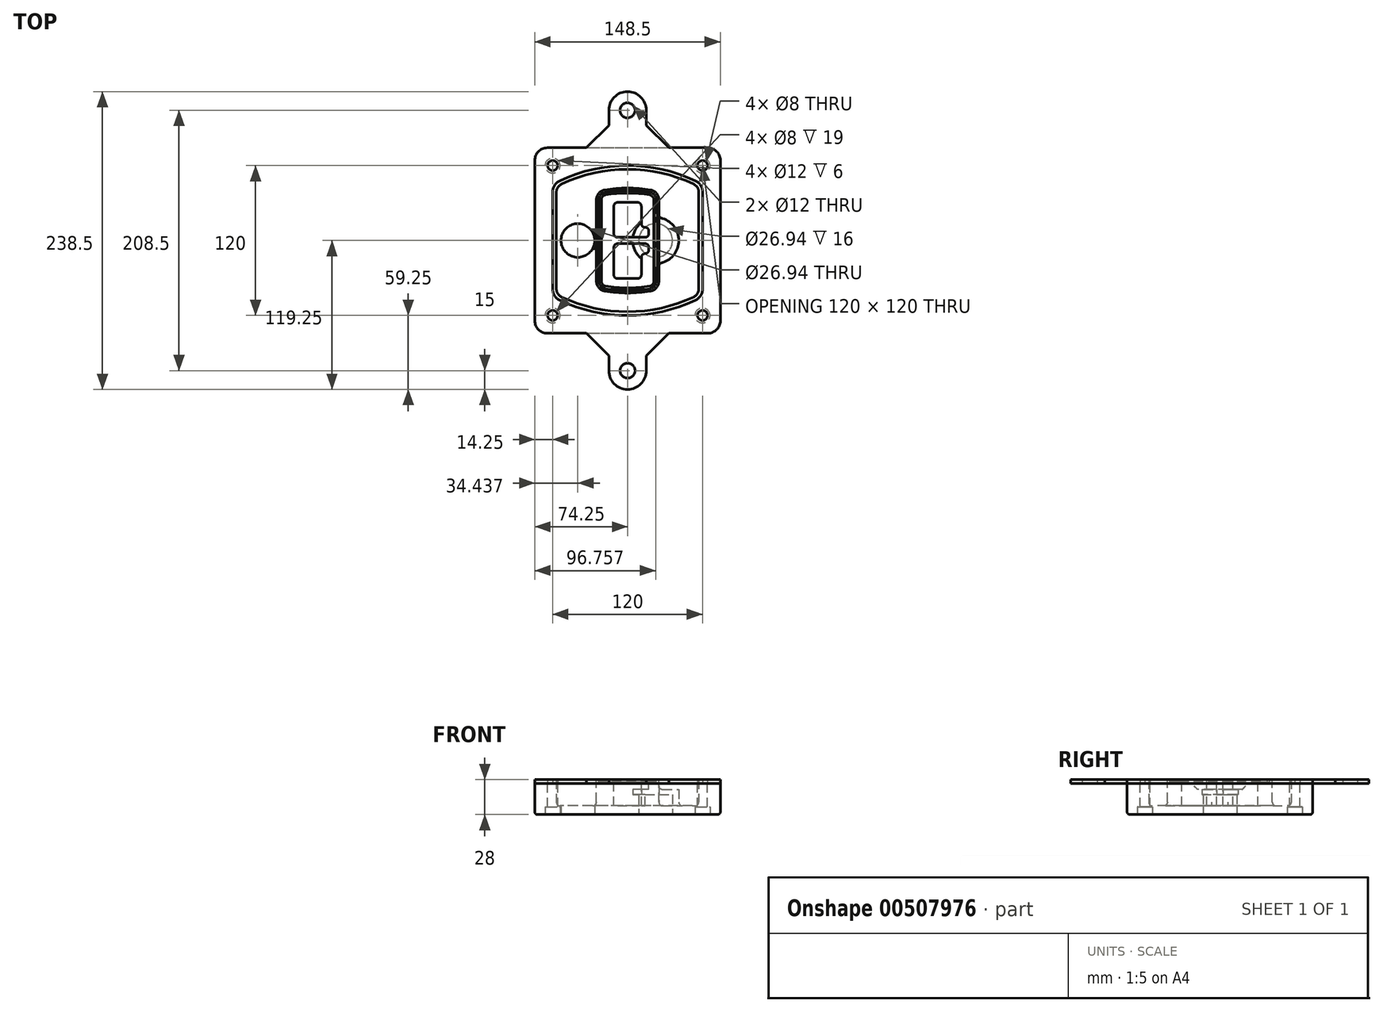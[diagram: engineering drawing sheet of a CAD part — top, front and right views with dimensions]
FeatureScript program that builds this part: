
annotation { "Feature Type Name" : "Feature", "Feature Type Description" : "" }
export const myFeature = defineFeature(function(context is Context, id is Id, definition is map)
    precondition{}
    {
        {
            var Q0;
            Q0=qCreatedBy(makeId("Top.planeOp"),FACE);
            var sketch = newSketch(context, id + "F0", { "sketchPlane" : qUnion([Q0])});
            skPoint(sketch, "E0.rect.middle", {"position": v(0, 0) * mm});
            skLineSegment(sketch, "E1.bottom", {"start": v(-64.25, -74.25) * mm, "end": v(64.25, -74.25) * mm});
            skLineSegment(sketch, "E1.top", {"start": v(-64.25, 74.25) * mm, "end": v(64.25, 74.25) * mm});
            skLineSegment(sketch, "E1.left", {"start": v(-74.25, -64.25) * mm, "end": v(-74.25, 64.25) * mm});
            skLineSegment(sketch, "E1.right", {"start": v(74.25, -64.25) * mm, "end": v(74.25, 64.25) * mm});
            skLineSegment(sketch, "E2", {"start": v(-74.25, 74.25) * mm, "end": v(74.25, -74.25) * mm, "construction": true});
            skLineSegment(sketch, "E3", {"start": v(74.25, 74.25) * mm, "end": v(-74.25, -74.25) * mm, "construction": true});
            skCircle(sketch, "E4", {"center": v(-60, 60) * mm, "radius": 4 * mm});
            skCircle(sketch, "E5", {"center": v(60, 60) * mm, "radius": 4 * mm});
            skCircle(sketch, "E6", {"center": v(60, -60) * mm, "radius": 4 * mm});
            skCircle(sketch, "E7", {"center": v(-60, -60) * mm, "radius": 4 * mm});
            skLineSegment(sketch, "E8", {"start": v(-60, 60) * mm, "end": v(60, 60) * mm, "construction": true});
            skLineSegment(sketch, "E9", {"start": v(60, 60) * mm, "end": v(60, -60) * mm, "construction": true});
            skLineSegment(sketch, "E10", {"start": v(60, -60) * mm, "end": v(-60, -60) * mm, "construction": true});
            skLineSegment(sketch, "E11", {"start": v(-60, -60) * mm, "end": v(-60, 60) * mm, "construction": true});
            skLineSegment(sketch, "E12", {"start": v(-60, 38.83) * mm, "end": v(-60, -38.83) * mm});
            skLineSegment(sketch, "E13", {"start": v(60, 38.83) * mm, "end": v(60, -38.83) * mm});
            skArc(sketch, "E14", {"start": v(54.26, 47.88) * mm, "mid": v(0, 60) * mm, "end": v(-54.26, 47.88) * mm});
            skArc(sketch, "E15", {"start": v(-54.26, -47.88) * mm, "mid": v(0, -60) * mm, "end": v(54.26, -47.88) * mm});
            skLineSegment(sketch, "E16", {"start": v(-60, 0) * mm, "end": v(60, 0) * mm, "construction": true});
            skPoint(sketch, "E17.visualSharp", {"position": v(-60, -45) * mm});
            skArc(sketch, "E17.filletArc", {"start": v(-60, -38.83) * mm, "mid": v(-58.44, -44.2) * mm, "end": v(-54.26, -47.88) * mm});
            skPoint(sketch, "E18.visualSharp", {"position": v(-60, 45) * mm});
            skArc(sketch, "E18.filletArc", {"start": v(-54.26, 47.88) * mm, "mid": v(-58.44, 44.2) * mm, "end": v(-60, 38.83) * mm});
            skPoint(sketch, "E19.visualSharp", {"position": v(60, 45) * mm});
            skArc(sketch, "E19.filletArc", {"start": v(60, 38.83) * mm, "mid": v(58.44, 44.2) * mm, "end": v(54.26, 47.88) * mm});
            skPoint(sketch, "E20.visualSharp", {"position": v(60, -45) * mm});
            skArc(sketch, "E20.filletArc", {"start": v(54.26, -47.88) * mm, "mid": v(58.44, -44.2) * mm, "end": v(60, -38.83) * mm});
            skPoint(sketch, "E21.visualSharp", {"position": v(-74.25, 74.25) * mm});
            skArc(sketch, "E21.filletArc", {"start": v(-64.25, 74.25) * mm, "mid": v(-71.32, 71.32) * mm, "end": v(-74.25, 64.25) * mm});
            skPoint(sketch, "E22.visualSharp", {"position": v(74.25, 74.25) * mm});
            skArc(sketch, "E22.filletArc", {"start": v(74.25, 64.25) * mm, "mid": v(71.32, 71.32) * mm, "end": v(64.25, 74.25) * mm});
            skPoint(sketch, "E23.visualSharp", {"position": v(74.25, -74.25) * mm});
            skArc(sketch, "E23.filletArc", {"start": v(64.25, -74.25) * mm, "mid": v(71.32, -71.32) * mm, "end": v(74.25, -64.25) * mm});
            skPoint(sketch, "E24.visualSharp", {"position": v(-74.25, -74.25) * mm});
            skArc(sketch, "E24.filletArc", {"start": v(-74.25, -64.25) * mm, "mid": v(-71.32, -71.32) * mm, "end": v(-64.25, -74.25) * mm});
            skArc(sketch, "E25.0", {"start": v(57, 38.83) * mm, "mid": v(55.9, 42.58) * mm, "end": v(52.98, 45.17) * mm});
            skLineSegment(sketch, "E25.1", {"start": v(57, 38.83) * mm, "end": v(57, -38.83) * mm});
            skArc(sketch, "E25.2", {"start": v(52.98, -45.17) * mm, "mid": v(55.9, -42.58) * mm, "end": v(57, -38.83) * mm});
            skArc(sketch, "E25.3", {"start": v(-52.98, -45.17) * mm, "mid": v(0, -57) * mm, "end": v(52.98, -45.17) * mm});
            skArc(sketch, "E25.4", {"start": v(-57, -38.83) * mm, "mid": v(-55.9, -42.58) * mm, "end": v(-52.98, -45.17) * mm});
            skArc(sketch, "E25.5", {"start": v(52.98, 45.17) * mm, "mid": v(0, 57) * mm, "end": v(-52.98, 45.17) * mm});
            skLineSegment(sketch, "E25.6", {"start": v(-57, 38.83) * mm, "end": v(-57, -38.83) * mm});
            skArc(sketch, "E25.7", {"start": v(-52.98, 45.17) * mm, "mid": v(-55.9, 42.58) * mm, "end": v(-57, 38.83) * mm});
            skArc(sketch, "E26.0", {"start": v(-55.96, 51.5) * mm, "mid": v(-61.82, 46.33) * mm, "end": v(-64, 38.83) * mm});
            skArc(sketch, "E26.1", {"start": v(55.96, 51.5) * mm, "mid": v(0, 64) * mm, "end": v(-55.96, 51.5) * mm});
            skArc(sketch, "E26.2", {"start": v(64, 38.83) * mm, "mid": v(61.82, 46.33) * mm, "end": v(55.96, 51.5) * mm});
            skLineSegment(sketch, "E26.3", {"start": v(64, 38.83) * mm, "end": v(64, -38.83) * mm});
            skArc(sketch, "E26.4", {"start": v(55.96, -51.5) * mm, "mid": v(61.82, -46.33) * mm, "end": v(64, -38.83) * mm});
            skLineSegment(sketch, "E26.5", {"start": v(-64, 38.83) * mm, "end": v(-64, -38.83) * mm});
            skArc(sketch, "E26.6", {"start": v(-55.96, -51.5) * mm, "mid": v(0, -64) * mm, "end": v(55.96, -51.5) * mm});
            skArc(sketch, "E26.7", {"start": v(-64, -38.83) * mm, "mid": v(-61.82, -46.33) * mm, "end": v(-55.96, -51.5) * mm});
            skSolve(sketch);
        }
        {
            var Q0;
            Q0=makeQuery(id+"F0.imprint","IMPRINT",FACE,{"disambiguationData":[TD([[makeQuery(id+"F0.imprint","IMPRINT",EDGE,{"derivedFrom":sQuery(id+"F0.wireOp",EDGE,"E1.bottom")}),1.0]])]});
            var Q1;
            Q1=makeQuery(id+"F0.imprint","IMPRINT",FACE,{"disambiguationData":[TD([[makeQuery(id+"F0.imprint","IMPRINT",EDGE,{"derivedFrom":sQuery(id+"F0.wireOp",EDGE,"E12")}),1.0]])]});
            var Q2;
            Q2=makeQuery(id+"F0.imprint","IMPRINT",FACE,{"disambiguationData":[TD([[makeQuery(id+"F0.imprint","IMPRINT",EDGE,{"derivedFrom":sQuery(id+"F0.wireOp",EDGE,"E25.0")}),1.0]])]});
            var Q3;
            Q3=makeQuery(id+"F0.imprint","IMPRINT",FACE,{"disambiguationData":[TD([[makeQuery(id+"F0.imprint","IMPRINT",EDGE,{"derivedFrom":sQuery(id+"F0.wireOp",EDGE,"E12")}),-1.0]])]});
            extrude(context, id + "F1", {"entities" : qUnion([Q0, Q1, Q2, Q3]), "oppositeDirection" : true, "depth" : 25 * mm});
        }
        {
            var Q0;
            Q0=makeQuery(id+"F0.imprint","IMPRINT",FACE,{"disambiguationData":[TD([[makeQuery(id+"F0.imprint","IMPRINT",EDGE,{"derivedFrom":sQuery(id+"F0.wireOp",EDGE,"E12")}),1.0]])]});
            extrude(context, id + "F2", {"entities" : qUnion([Q0]), "operationType" : NewBodyOperationType.ADD, "depth" : 3 * mm});
        }
        {
            var Q0;
            Q0=makeQuery(id+"F0.imprint","IMPRINT",FACE,{"disambiguationData":[TD([[makeQuery(id+"F0.imprint","IMPRINT",EDGE,{"derivedFrom":sQuery(id+"F0.wireOp",EDGE,"E25.0")}),1.0]])]});
            extrude(context, id + "F3", {"entities" : qUnion([Q0]), "operationType" : NewBodyOperationType.REMOVE, "oppositeDirection" : true, "depth" : 18 * mm});
        }
        {
            var Q0;
            Q0=makeQuery(id+"F2.opExtrude","CAP_FACE",FACE,{"disambiguationData":[OSD([sQuery(id+"F0.wireOp",EDGE,"E12"),sQuery(id+"F0.wireOp",EDGE,"E13"),sQuery(id+"F0.wireOp",EDGE,"E14"),sQuery(id+"F0.wireOp",EDGE,"E15"),sQuery(id+"F0.wireOp",EDGE,"E17.filletArc"),sQuery(id+"F0.wireOp",EDGE,"E18.filletArc"),sQuery(id+"F0.wireOp",EDGE,"E19.filletArc"),sQuery(id+"F0.wireOp",EDGE,"E20.filletArc"),sQuery(id+"F0.wireOp",EDGE,"E25.0"),sQuery(id+"F0.wireOp",EDGE,"E25.1"),sQuery(id+"F0.wireOp",EDGE,"E25.2"),sQuery(id+"F0.wireOp",EDGE,"E25.3"),sQuery(id+"F0.wireOp",EDGE,"E25.4"),sQuery(id+"F0.wireOp",EDGE,"E25.5"),sQuery(id+"F0.wireOp",EDGE,"E25.6"),sQuery(id+"F0.wireOp",EDGE,"E25.7")])],"isStart":false});
            var sketch = newSketch(context, id + "F4", { "sketchPlane" : qUnion([Q0])});
            skArc(sketch, "E27.0", {"start": v(-18.34, -40.45) * mm, "mid": v(0, -42) * mm, "end": v(18.34, -40.45) * mm});
            skArc(sketch, "E28.0", {"start": v(18.34, 40.45) * mm, "mid": v(0, 42) * mm, "end": v(-18.34, 40.45) * mm});
            skLineSegment(sketch, "E29", {"start": v(-25, 32.57) * mm, "end": v(-25, -32.57) * mm});
            skLineSegment(sketch, "E30", {"start": v(25, 32.57) * mm, "end": v(25, -32.57) * mm});
            skLineSegment(sketch, "E31", {"start": v(-25, 39.1) * mm, "end": v(25, 39.1) * mm, "construction": true});
            skLineSegment(sketch, "E32", {"start": v(-25, -39.1) * mm, "end": v(25, -39.1) * mm, "construction": true});
            skPoint(sketch, "E33.visualSharp", {"position": v(-25, 39.1) * mm});
            skArc(sketch, "E33.filletArc", {"start": v(-18.34, 40.45) * mm, "mid": v(-23.11, 37.73) * mm, "end": v(-25, 32.57) * mm});
            skPoint(sketch, "E34.visualSharp", {"position": v(25, 39.1) * mm});
            skArc(sketch, "E34.filletArc", {"start": v(25, 32.57) * mm, "mid": v(23.11, 37.73) * mm, "end": v(18.34, 40.45) * mm});
            skPoint(sketch, "E35.visualSharp", {"position": v(25, -39.1) * mm});
            skArc(sketch, "E35.filletArc", {"start": v(18.34, -40.45) * mm, "mid": v(23.11, -37.73) * mm, "end": v(25, -32.57) * mm});
            skPoint(sketch, "E36.visualSharp", {"position": v(-25, -39.1) * mm});
            skArc(sketch, "E36.filletArc", {"start": v(-25, -32.57) * mm, "mid": v(-23.11, -37.73) * mm, "end": v(-18.34, -40.45) * mm});
            skArc(sketch, "E37.0", {"start": v(52.98, 45.17) * mm, "mid": v(0, 57) * mm, "end": v(-52.98, 45.17) * mm});
            skArc(sketch, "E37.1", {"start": v(-52.98, 45.17) * mm, "mid": v(-55.9, 42.58) * mm, "end": v(-57, 38.83) * mm});
            skLineSegment(sketch, "E37.2", {"start": v(-57, 38.83) * mm, "end": v(-57, -38.83) * mm});
            skArc(sketch, "E37.3", {"start": v(-57, -38.83) * mm, "mid": v(-55.9, -42.58) * mm, "end": v(-52.98, -45.17) * mm});
            skArc(sketch, "E37.4", {"start": v(-52.98, -45.17) * mm, "mid": v(0, -57) * mm, "end": v(52.98, -45.17) * mm});
            skArc(sketch, "E37.5", {"start": v(52.98, -45.17) * mm, "mid": v(55.9, -42.58) * mm, "end": v(57, -38.83) * mm});
            skLineSegment(sketch, "E37.6", {"start": v(57, 38.83) * mm, "end": v(57, -38.83) * mm});
            skArc(sketch, "E37.7", {"start": v(57, 38.83) * mm, "mid": v(55.9, 42.58) * mm, "end": v(52.98, 45.17) * mm});
            skLineSegment(sketch, "E38.0", {"start": v(23, 32.57) * mm, "end": v(23, -32.57) * mm});
            skArc(sketch, "E38.1", {"start": v(18, -38.48) * mm, "mid": v(21.58, -36.44) * mm, "end": v(23, -32.57) * mm});
            skArc(sketch, "E38.2", {"start": v(-18, -38.48) * mm, "mid": v(0, -40) * mm, "end": v(18, -38.48) * mm});
            skArc(sketch, "E38.3", {"start": v(-23, -32.57) * mm, "mid": v(-21.58, -36.44) * mm, "end": v(-18, -38.48) * mm});
            skLineSegment(sketch, "E38.4", {"start": v(-23, 32.57) * mm, "end": v(-23, -32.57) * mm});
            skArc(sketch, "E38.5", {"start": v(23, 32.57) * mm, "mid": v(21.58, 36.44) * mm, "end": v(18, 38.48) * mm});
            skArc(sketch, "E38.6", {"start": v(-18, 38.48) * mm, "mid": v(-21.58, 36.44) * mm, "end": v(-23, 32.57) * mm});
            skArc(sketch, "E38.7", {"start": v(18, 38.48) * mm, "mid": v(0, 40) * mm, "end": v(-18, 38.48) * mm});
            skArc(sketch, "E39.0", {"start": v(21, 32.57) * mm, "mid": v(20.06, 35.15) * mm, "end": v(17.67, 36.5) * mm});
            skLineSegment(sketch, "E39.1", {"start": v(21, 32.57) * mm, "end": v(21, -32.57) * mm});
            skArc(sketch, "E39.2", {"start": v(17.67, -36.5) * mm, "mid": v(20.06, -35.15) * mm, "end": v(21, -32.57) * mm});
            skArc(sketch, "E39.3", {"start": v(-17.67, -36.5) * mm, "mid": v(0, -38) * mm, "end": v(17.67, -36.5) * mm});
            skArc(sketch, "E39.4", {"start": v(-21, -32.57) * mm, "mid": v(-20.06, -35.15) * mm, "end": v(-17.67, -36.5) * mm});
            skArc(sketch, "E39.5", {"start": v(17.67, 36.5) * mm, "mid": v(0, 38) * mm, "end": v(-17.67, 36.5) * mm});
            skLineSegment(sketch, "E39.6", {"start": v(-21, 32.57) * mm, "end": v(-21, -32.57) * mm});
            skArc(sketch, "E39.7", {"start": v(-17.67, 36.5) * mm, "mid": v(-20.06, 35.15) * mm, "end": v(-21, 32.57) * mm});
            skLineSegment(sketch, "E40", {"start": v(-25, 0) * mm, "end": v(25, 0) * mm, "construction": true});
            skLineSegment(sketch, "E41", {"start": v(-11, 5.5) * mm, "end": v(-11, 27.5) * mm});
            skLineSegment(sketch, "E42", {"start": v(-8, 30.5) * mm, "end": v(8, 30.5) * mm});
            skLineSegment(sketch, "E43", {"start": v(11, 27.5) * mm, "end": v(11, 13.5) * mm});
            skLineSegment(sketch, "E44", {"start": v(14, 10.5) * mm, "end": v(14, 10.5) * mm});
            skLineSegment(sketch, "E45", {"start": v(17, 7.5) * mm, "end": v(17, 5.5) * mm});
            skLineSegment(sketch, "E46", {"start": v(14, 2.5) * mm, "end": v(-8, 2.5) * mm});
            skPoint(sketch, "E47.visualSharp", {"position": v(-11, 30.5) * mm});
            skArc(sketch, "E47.filletArc", {"start": v(-8, 30.5) * mm, "mid": v(-10.12, 29.62) * mm, "end": v(-11, 27.5) * mm});
            skPoint(sketch, "E48.visualSharp", {"position": v(11, 30.5) * mm});
            skArc(sketch, "E48.filletArc", {"start": v(11, 27.5) * mm, "mid": v(10.12, 29.62) * mm, "end": v(8, 30.5) * mm});
            skPoint(sketch, "E49.visualSharp", {"position": v(11, 10.5) * mm});
            skArc(sketch, "E49.filletArc", {"start": v(11, 13.5) * mm, "mid": v(11.88, 11.38) * mm, "end": v(14, 10.5) * mm});
            skPoint(sketch, "E50.visualSharp", {"position": v(17, 10.5) * mm});
            skArc(sketch, "E50.filletArc", {"start": v(17, 7.5) * mm, "mid": v(16.12, 9.62) * mm, "end": v(14, 10.5) * mm});
            skPoint(sketch, "E51.visualSharp", {"position": v(17, 2.5) * mm});
            skArc(sketch, "E51.filletArc", {"start": v(14, 2.5) * mm, "mid": v(16.12, 3.38) * mm, "end": v(17, 5.5) * mm});
            skPoint(sketch, "E52.visualSharp", {"position": v(-11, 2.5) * mm});
            skArc(sketch, "E52.filletArc", {"start": v(-11, 5.5) * mm, "mid": v(-10.12, 3.38) * mm, "end": v(-8, 2.5) * mm});
            skLineSegment(sketch, "E53.0.MirrorCS", {"start": v(14, -2.5) * mm, "end": v(-8, -2.5) * mm});
            skArc(sketch, "E54.0.MirrorCS", {"start": v(-11, -5.5) * mm, "mid": v(-10.12, -3.38) * mm, "end": v(-8, -2.5) * mm});
            skLineSegment(sketch, "E55.0.MirrorCS", {"start": v(-11, -5.5) * mm, "end": v(-11, -27.5) * mm});
            skArc(sketch, "E56.0.MirrorCS", {"start": v(-8, -30.5) * mm, "mid": v(-10.12, -29.62) * mm, "end": v(-11, -27.5) * mm});
            skLineSegment(sketch, "E57.0.MirrorCS", {"start": v(-8, -30.5) * mm, "end": v(8, -30.5) * mm});
            skArc(sketch, "E58.0.MirrorCS", {"start": v(11, -27.5) * mm, "mid": v(10.12, -29.62) * mm, "end": v(8, -30.5) * mm});
            skLineSegment(sketch, "E59.0.MirrorCS", {"start": v(11, -27.5) * mm, "end": v(11, -13.5) * mm});
            skArc(sketch, "E60.0.MirrorCS", {"start": v(11, -13.5) * mm, "mid": v(11.88, -11.38) * mm, "end": v(14, -10.5) * mm});
            skArc(sketch, "E61.0.MirrorCS", {"start": v(17, -7.5) * mm, "mid": v(16.12, -9.62) * mm, "end": v(14, -10.5) * mm});
            skLineSegment(sketch, "E62.0.MirrorCS", {"start": v(17, -7.5) * mm, "end": v(17, -5.5) * mm});
            skArc(sketch, "E63.0.MirrorCS", {"start": v(14, -2.5) * mm, "mid": v(16.12, -3.38) * mm, "end": v(17, -5.5) * mm});
            skSolve(sketch);
        }
        {
            var Q0;
            Q0=makeQuery(id+"F4.imprint","IMPRINT",FACE,{"disambiguationData":[TD([[makeQuery(id+"F4.imprint","IMPRINT",EDGE,{"derivedFrom":sQuery(id+"F4.wireOp",EDGE,"E27.0")}),1.0]])]});
            var Q1;
            Q1=makeQuery(id+"F4.imprint","IMPRINT",FACE,{"disambiguationData":[TD([[makeQuery(id+"F4.imprint","IMPRINT",EDGE,{"derivedFrom":sQuery(id+"F4.wireOp",EDGE,"E38.0")}),-1.0]])]});
            var Q2;
            Q2=makeQuery(id+"F4.imprint","IMPRINT",FACE,{"disambiguationData":[TD([[makeQuery(id+"F4.imprint","IMPRINT",EDGE,{"derivedFrom":sQuery(id+"F4.wireOp",EDGE,"E39.0")}),1.0]])]});
            extrude(context, id + "F5", {"entities" : qUnion([Q0, Q1, Q2]), "operationType" : NewBodyOperationType.ADD, "endBound" : BoundingType.UP_TO_NEXT, "oppositeDirection" : true, "depth" : 25 * mm});
        }
        {
            var Q0;
            Q0=makeQuery(id+"F4.imprint","IMPRINT",FACE,{"disambiguationData":[TD([[makeQuery(id+"F4.imprint","IMPRINT",EDGE,{"derivedFrom":sQuery(id+"F4.wireOp",EDGE,"E38.0")}),-1.0]])]});
            extrude(context, id + "F6", {"entities" : qUnion([Q0]), "operationType" : NewBodyOperationType.REMOVE, "oppositeDirection" : true, "depth" : 2 * mm});
        }
        {
            var Q0;
            Q0=makeQuery(id+"F1.opExtrude","CAP_FACE",FACE,{"disambiguationData":[OSD([sQuery(id+"F0.wireOp",EDGE,"E1.bottom"),sQuery(id+"F0.wireOp",EDGE,"E1.top"),sQuery(id+"F0.wireOp",EDGE,"E1.left"),sQuery(id+"F0.wireOp",EDGE,"E1.right"),sQuery(id+"F0.wireOp",EDGE,"E4"),sQuery(id+"F0.wireOp",EDGE,"E5"),sQuery(id+"F0.wireOp",EDGE,"E6"),sQuery(id+"F0.wireOp",EDGE,"E7"),sQuery(id+"F0.wireOp",EDGE,"E21.filletArc"),sQuery(id+"F0.wireOp",EDGE,"E22.filletArc"),sQuery(id+"F0.wireOp",EDGE,"E23.filletArc"),sQuery(id+"F0.wireOp",EDGE,"E24.filletArc")])],"isStart":false});
            var sketch = newSketch(context, id + "F7", { "sketchPlane" : qUnion([Q0])});
            skCircle(sketch, "E64", {"center": v(22.5, 0) * mm, "radius": 13.47 * mm});
            skCircle(sketch, "E65", {"center": v(-39.81, 0) * mm, "radius": 13.47 * mm});
            skLineSegment(sketch, "E66", {"start": v(74.25, 0) * mm, "end": v(-74.25, 0) * mm});
            skCircle(sketch, "E67", {"center": v(22.5, 0) * mm, "radius": 18.47 * mm});
            skCircle(sketch, "E68", {"center": v(60, -60) * mm, "radius": 6 * mm});
            skCircle(sketch, "E69", {"center": v(-60, -60) * mm, "radius": 6 * mm});
            skCircle(sketch, "E70", {"center": v(-60, 60) * mm, "radius": 6 * mm});
            skCircle(sketch, "E71", {"center": v(60, 60) * mm, "radius": 6 * mm});
            skSolve(sketch);
        }
        {
            var Q0;
            {var subQ1=sQuery(id+"F7.wireOp",EDGE,"E66");var subQ4=sQuery(id+"F7.wireOp",EDGE,"E64");var subQ6=makeQuery(id+"F7.imprint","INTERSECT",VERTEX,{"disambiguationData":[OD(0.0)],"derivedFrom":[subQ4,subQ1]});Q0=makeQuery(id+"F7.imprint","IMPRINT",FACE,{"disambiguationData":[TD([[makeQuery(id+"F7.imprint","IMPRINT",EDGE,{"disambiguationData":[TD([[subQ6,-1.0]])],"derivedFrom":subQ4}),-1.0]])]});}
            var Q1;
            {var subQ0=sQuery(id+"F7.wireOp",EDGE,"E66");var subQ1=sQuery(id+"F7.wireOp",EDGE,"E64");var subQ3=makeQuery(id+"F7.imprint","INTERSECT",VERTEX,{"disambiguationData":[OD(0.0)],"derivedFrom":[subQ1,subQ0]});Q1=makeQuery(id+"F7.imprint","IMPRINT",FACE,{"disambiguationData":[TD([[makeQuery(id+"F7.imprint","IMPRINT",EDGE,{"disambiguationData":[TD([[subQ3,-1.0]])],"derivedFrom":subQ1}),1.0]])]});}
            var Q2;
            {var subQ0=sQuery(id+"F7.wireOp",EDGE,"E66");var subQ1=sQuery(id+"F7.wireOp",EDGE,"E64");var subQ3=makeQuery(id+"F7.imprint","INTERSECT",VERTEX,{"disambiguationData":[OD(0.0)],"derivedFrom":[subQ1,subQ0]});Q2=makeQuery(id+"F7.imprint","IMPRINT",FACE,{"disambiguationData":[TD([[makeQuery(id+"F7.imprint","IMPRINT",EDGE,{"disambiguationData":[TD([[subQ3,1.0]])],"derivedFrom":subQ1}),1.0]])]});}
            var Q3;
            {var subQ1=sQuery(id+"F7.wireOp",EDGE,"E66");var subQ4=sQuery(id+"F7.wireOp",EDGE,"E64");var subQ6=makeQuery(id+"F7.imprint","INTERSECT",VERTEX,{"disambiguationData":[OD(0.0)],"derivedFrom":[subQ4,subQ1]});Q3=makeQuery(id+"F7.imprint","IMPRINT",FACE,{"disambiguationData":[TD([[makeQuery(id+"F7.imprint","IMPRINT",EDGE,{"disambiguationData":[TD([[subQ6,1.0]])],"derivedFrom":subQ4}),-1.0]])]});}
            extrude(context, id + "F8", {"entities" : qUnion([Q0, Q1, Q2, Q3]), "operationType" : NewBodyOperationType.ADD, "oppositeDirection" : true, "depth" : 20 * mm});
        }
        {
            var Q0;
            {var subQ0=sQuery(id+"F7.wireOp",EDGE,"E66");var subQ1=sQuery(id+"F7.wireOp",EDGE,"E64");var subQ3=makeQuery(id+"F7.imprint","INTERSECT",VERTEX,{"disambiguationData":[OD(0.0)],"derivedFrom":[subQ1,subQ0]});Q0=makeQuery(id+"F7.imprint","IMPRINT",FACE,{"disambiguationData":[TD([[makeQuery(id+"F7.imprint","IMPRINT",EDGE,{"disambiguationData":[TD([[subQ3,-1.0]])],"derivedFrom":subQ1}),1.0]])]});}
            var Q1;
            {var subQ0=sQuery(id+"F7.wireOp",EDGE,"E66");var subQ1=sQuery(id+"F7.wireOp",EDGE,"E64");var subQ3=makeQuery(id+"F7.imprint","INTERSECT",VERTEX,{"disambiguationData":[OD(0.0)],"derivedFrom":[subQ1,subQ0]});Q1=makeQuery(id+"F7.imprint","IMPRINT",FACE,{"disambiguationData":[TD([[makeQuery(id+"F7.imprint","IMPRINT",EDGE,{"disambiguationData":[TD([[subQ3,1.0]])],"derivedFrom":subQ1}),1.0]])]});}
            extrude(context, id + "F9", {"entities" : qUnion([Q0, Q1]), "operationType" : NewBodyOperationType.REMOVE, "oppositeDirection" : true, "depth" : 16 * mm});
        }
        {
            var Q0;
            {var subQ0=sQuery(id+"F7.wireOp",EDGE,"E66");var subQ1=sQuery(id+"F7.wireOp",EDGE,"E65");var subQ3=makeQuery(id+"F7.imprint","INTERSECT",VERTEX,{"disambiguationData":[OD(0.0)],"derivedFrom":[subQ1,subQ0]});Q0=makeQuery(id+"F7.imprint","IMPRINT",FACE,{"disambiguationData":[TD([[makeQuery(id+"F7.imprint","IMPRINT",EDGE,{"disambiguationData":[TD([[subQ3,-1.0]])],"derivedFrom":subQ1}),1.0]])]});}
            var Q1;
            {var subQ0=sQuery(id+"F7.wireOp",EDGE,"E66");var subQ1=sQuery(id+"F7.wireOp",EDGE,"E65");var subQ3=makeQuery(id+"F7.imprint","INTERSECT",VERTEX,{"disambiguationData":[OD(0.0)],"derivedFrom":[subQ1,subQ0]});Q1=makeQuery(id+"F7.imprint","IMPRINT",FACE,{"disambiguationData":[TD([[makeQuery(id+"F7.imprint","IMPRINT",EDGE,{"disambiguationData":[TD([[subQ3,1.0]])],"derivedFrom":subQ1}),1.0]])]});}
            extrude(context, id + "F10", {"entities" : qUnion([Q0, Q1]), "operationType" : NewBodyOperationType.REMOVE, "oppositeDirection" : true, "depth" : 25 * mm});
        }
        {
            var Q0;
            Q0=makeQuery(id+"F7.imprint","IMPRINT",FACE,{"disambiguationData":[TD([[makeQuery(id+"F7.imprint","IMPRINT",EDGE,{"derivedFrom":sQuery(id+"F7.wireOp",EDGE,"E68")}),1.0]])]});
            var Q1;
            Q1=makeQuery(id+"F7.imprint","IMPRINT",FACE,{"disambiguationData":[TD([[makeQuery(id+"F7.imprint","IMPRINT",EDGE,{"derivedFrom":makeQuery(id+"F1.opExtrude","CAP_EDGE",EDGE,{"disambiguationData":[OSD([sQuery(id+"F0.wireOp",EDGE,"E5")])],"isStart":false})}),-1.0]])]});
            var Q2;
            Q2=makeQuery(id+"F7.imprint","IMPRINT",FACE,{"disambiguationData":[TD([[makeQuery(id+"F7.imprint","IMPRINT",EDGE,{"derivedFrom":sQuery(id+"F7.wireOp",EDGE,"E69")}),1.0]])]});
            var Q3;
            Q3=makeQuery(id+"F7.imprint","IMPRINT",FACE,{"disambiguationData":[TD([[makeQuery(id+"F7.imprint","IMPRINT",EDGE,{"derivedFrom":makeQuery(id+"F1.opExtrude","CAP_EDGE",EDGE,{"disambiguationData":[OSD([sQuery(id+"F0.wireOp",EDGE,"E4")])],"isStart":false})}),-1.0]])]});
            var Q4;
            Q4=makeQuery(id+"F7.imprint","IMPRINT",FACE,{"disambiguationData":[TD([[makeQuery(id+"F7.imprint","IMPRINT",EDGE,{"derivedFrom":sQuery(id+"F7.wireOp",EDGE,"E70")}),1.0]])]});
            var Q5;
            Q5=makeQuery(id+"F7.imprint","IMPRINT",FACE,{"disambiguationData":[TD([[makeQuery(id+"F7.imprint","IMPRINT",EDGE,{"derivedFrom":makeQuery(id+"F1.opExtrude","CAP_EDGE",EDGE,{"disambiguationData":[OSD([sQuery(id+"F0.wireOp",EDGE,"E7")])],"isStart":false})}),-1.0]])]});
            var Q6;
            Q6=makeQuery(id+"F7.imprint","IMPRINT",FACE,{"disambiguationData":[TD([[makeQuery(id+"F7.imprint","IMPRINT",EDGE,{"derivedFrom":sQuery(id+"F7.wireOp",EDGE,"E71")}),1.0]])]});
            var Q7;
            Q7=makeQuery(id+"F7.imprint","IMPRINT",FACE,{"disambiguationData":[TD([[makeQuery(id+"F7.imprint","IMPRINT",EDGE,{"derivedFrom":makeQuery(id+"F1.opExtrude","CAP_EDGE",EDGE,{"disambiguationData":[OSD([sQuery(id+"F0.wireOp",EDGE,"E6")])],"isStart":false})}),-1.0]])]});
            extrude(context, id + "F11", {"entities" : qUnion([Q0, Q1, Q2, Q3, Q4, Q5, Q6, Q7]), "operationType" : NewBodyOperationType.REMOVE, "oppositeDirection" : true, "depth" : 6 * mm});
        }
        {
            var Q0;
            Q0=makeQuery(id+"F9.boolean.opBoolean","COPY",FACE,{"derivedFrom":makeQuery(id+"F9.opExtrude","CAP_FACE",FACE,{"disambiguationData":[OSD([sQuery(id+"F7.wireOp",EDGE,"E64")])],"isStart":false})});
            var sketch = newSketch(context, id + "F12", { "sketchPlane" : qUnion([Q0])});
            skArc(sketch, "E72.0", {"start": v(11, 14.45) * mm, "mid": v(6.45, 9.13) * mm, "end": v(4.2, 2.5) * mm});
            skArc(sketch, "E72.1", {"start": v(4.2, -2.5) * mm, "mid": v(6.45, -9.13) * mm, "end": v(11, -14.45) * mm});
            skLineSegment(sketch, "E73", {"start": v(4.2, -2.5) * mm, "end": v(14, -2.5) * mm});
            skLineSegment(sketch, "E74.0", {"start": v(14, 2.5) * mm, "end": v(4.2, 2.5) * mm});
            skArc(sketch, "E74.1", {"start": v(14, 2.5) * mm, "mid": v(16.12, 3.38) * mm, "end": v(17, 5.5) * mm});
            skLineSegment(sketch, "E74.2", {"start": v(17, 7.5) * mm, "end": v(17, 5.5) * mm});
            skArc(sketch, "E74.3", {"start": v(17, 7.5) * mm, "mid": v(16.12, 9.62) * mm, "end": v(14, 10.5) * mm});
            skArc(sketch, "E74.4", {"start": v(11, 13.5) * mm, "mid": v(11.88, 11.38) * mm, "end": v(14, 10.5) * mm});
            skLineSegment(sketch, "E74.5", {"start": v(11, 14.45) * mm, "end": v(11, 13.5) * mm});
            skLineSegment(sketch, "E74.7", {"start": v(14, -2.5) * mm, "end": v(4.2, -2.5) * mm});
            skArc(sketch, "E74.8", {"start": v(14, -2.5) * mm, "mid": v(16.12, -3.38) * mm, "end": v(17, -5.5) * mm});
            skLineSegment(sketch, "E74.9", {"start": v(17, -7.5) * mm, "end": v(17, -5.5) * mm});
            skArc(sketch, "E74.10", {"start": v(17, -7.5) * mm, "mid": v(16.12, -9.62) * mm, "end": v(14, -10.5) * mm});
            skArc(sketch, "E74.11", {"start": v(11, -13.5) * mm, "mid": v(11.88, -11.38) * mm, "end": v(14, -10.5) * mm});
            skLineSegment(sketch, "E74.12", {"start": v(11, -14.45) * mm, "end": v(11, -13.5) * mm});
            skPoint(sketch, "E75.orphan", {"position": v(11, -27.5) * mm});
            skPoint(sketch, "E76.orphan", {"position": v(-8, -2.5) * mm});
            skPoint(sketch, "E77.orphan", {"position": v(-8, 2.5) * mm});
            skPoint(sketch, "E78.orphan", {"position": v(11, 27.5) * mm});
            skSolve(sketch);
        }
        {
            var Q0;
            {var subQ7=sQuery(id+"F12.wireOp",EDGE,"E72.0");var subQ14=sQuery(id+"F12.wireOp",EDGE,"E72.1");var subQ16=sQuery(id+"F12.wireOp",EDGE,"E74.1");var subQ18=sQuery(id+"F12.wireOp",EDGE,"E74.8");Q0=qUnion([makeQuery(id+"F12.imprint","IMPRINT",FACE,{"disambiguationData":[TD([[makeQuery(id+"F12.imprint","IMPRINT",EDGE,{"derivedFrom":subQ7}),1.0]])]}),makeQuery(id+"F12.imprint","IMPRINT",FACE,{"disambiguationData":[TD([[makeQuery(id+"F12.imprint","IMPRINT",EDGE,{"derivedFrom":subQ14}),1.0]])]}),makeQuery(id+"F12.imprint","IMPRINT",FACE,{"disambiguationData":[TD([[makeQuery(id+"F12.imprint","IMPRINT",EDGE,{"derivedFrom":subQ16}),1.0]])]}),makeQuery(id+"F12.imprint","IMPRINT",FACE,{"disambiguationData":[TD([[makeQuery(id+"F12.imprint","IMPRINT",EDGE,{"derivedFrom":subQ18}),-1.0]])]})]);}
            var Q1;
            Q1=makeQuery(id+"F5.boolean.opBoolean","SPLIT",FACE,{"disambiguationData":[TD([makeQuery(id+"F5.opExtrude","SWEPT_FACE",FACE,{"disambiguationData":[OSD([sQuery(id+"F4.wireOp",EDGE,"E41")])]})])],"derivedFrom":makeQuery(id+"F3.boolean.opBoolean","COPY",FACE,{"derivedFrom":makeQuery(id+"F3.opExtrude","CAP_FACE",FACE,{"disambiguationData":[OSD([sQuery(id+"F0.wireOp",EDGE,"E25.0"),sQuery(id+"F0.wireOp",EDGE,"E25.1"),sQuery(id+"F0.wireOp",EDGE,"E25.2"),sQuery(id+"F0.wireOp",EDGE,"E25.3"),sQuery(id+"F0.wireOp",EDGE,"E25.4"),sQuery(id+"F0.wireOp",EDGE,"E25.5"),sQuery(id+"F0.wireOp",EDGE,"E25.6"),sQuery(id+"F0.wireOp",EDGE,"E25.7")])],"isStart":false})})});
            extrude(context, id + "F13", {"entities" : qUnion([Q0]), "operationType" : NewBodyOperationType.REMOVE, "endBound" : BoundingType.UP_TO_SURFACE, "endBoundEntityFace" : qUnion([Q1]), "depth" : 25 * mm});
        }
        {
            var Q0;
            Q0=makeQuery(id+"F3.boolean.opBoolean","COPY",EDGE,{"derivedFrom":makeQuery(id+"F3.opExtrude","CAP_EDGE",EDGE,{"disambiguationData":[OSD([sQuery(id+"F0.wireOp",EDGE,"E25.6")])],"isStart":false})});
            var Q1;
            Q1=makeQuery(id+"F8.boolean.opBoolean","INTERSECT",EDGE,{"derivedFrom":[makeQuery(id+"F5.opExtrude","SWEPT_FACE",FACE,{"disambiguationData":[OSD([sQuery(id+"F4.wireOp",EDGE,"E30")])]}),makeQuery(id+"F8.opExtrude","CAP_FACE",FACE,{"disambiguationData":[OSD([sQuery(id+"F7.wireOp",EDGE,"E67")])],"isStart":false})]});
            var Q2;
            Q2=makeQuery(id+"F8.boolean.opBoolean","INTERSECT",EDGE,{"disambiguationData":[OD(1.0)],"derivedFrom":[makeQuery(id+"F5.opExtrude","SWEPT_FACE",FACE,{"disambiguationData":[OSD([sQuery(id+"F4.wireOp",EDGE,"E30")])]}),makeQuery(id+"F8.opExtrude","SWEPT_FACE",FACE,{"disambiguationData":[OSD([sQuery(id+"F7.wireOp",EDGE,"E67")])]})]});
            var Q3;
            {var subQ0=sQuery(id+"F4.wireOp",EDGE,"E30");Q3=makeQuery(id+"F8.boolean.opBoolean","SPLIT",EDGE,{"disambiguationData":[TD([makeQuery(id+"F5.opExtrude","SWEPT_FACE",FACE,{"disambiguationData":[OSD([sQuery(id+"F4.wireOp",EDGE,"E35.filletArc")])]})])],"derivedFrom":makeQuery(id+"F5.opExtrude","CAP_EDGE",EDGE,{"disambiguationData":[OSD([subQ0])],"isStart":false})});}
            var Q4;
            {var subQ0=sQuery(id+"F0.wireOp",EDGE,"E25.7");var subQ1=sQuery(id+"F0.wireOp",EDGE,"E25.1");var subQ2=sQuery(id+"F0.wireOp",EDGE,"E25.6");var subQ3=sQuery(id+"F0.wireOp",EDGE,"E25.5");var subQ4=sQuery(id+"F0.wireOp",EDGE,"E25.4");var subQ5=sQuery(id+"F0.wireOp",EDGE,"E25.0");var subQ6=sQuery(id+"F0.wireOp",EDGE,"E25.2");var subQ7=sQuery(id+"F0.wireOp",EDGE,"E25.3");Q4=makeQuery(id+"F8.boolean.opBoolean","INTERSECT",EDGE,{"derivedFrom":[makeQuery(id+"F5.boolean.opBoolean","SPLIT",FACE,{"disambiguationData":[TD([makeQuery(id+"F2.opExtrude","SWEPT_FACE",FACE,{"disambiguationData":[OSD([subQ5])]})])],"derivedFrom":makeQuery(id+"F3.boolean.opBoolean","COPY",FACE,{"derivedFrom":makeQuery(id+"F3.opExtrude","CAP_FACE",FACE,{"disambiguationData":[OSD([subQ5,subQ1,subQ6,subQ7,subQ4,subQ3,subQ2,subQ0])],"isStart":false})})}),makeQuery(id+"F8.opExtrude","SWEPT_FACE",FACE,{"disambiguationData":[OSD([sQuery(id+"F7.wireOp",EDGE,"E67")])]})]});}
            var Q5;
            Q5=makeQuery(id+"F8.boolean.opBoolean","INTERSECT",EDGE,{"disambiguationData":[OD(0.0)],"derivedFrom":[makeQuery(id+"F5.opExtrude","SWEPT_FACE",FACE,{"disambiguationData":[OSD([sQuery(id+"F4.wireOp",EDGE,"E30")])]}),makeQuery(id+"F8.opExtrude","SWEPT_FACE",FACE,{"disambiguationData":[OSD([sQuery(id+"F7.wireOp",EDGE,"E67")])]})]});
            fillet(context, id + "F14", {"entities" : qUnion([Q0, Q1, Q2, Q3, Q4, Q5]), "radius" : 3 * mm, "tangentPropagation" : true, "allowEdgeOverflow" : false});
        }
        {
            var Q0;
            Q0=makeQuery(id+"F1.opExtrude","CAP_EDGE",EDGE,{"disambiguationData":[OSD([sQuery(id+"F0.wireOp",EDGE,"E1.bottom")])],"isStart":false});
            fillet(context, id + "F15", {"entities" : qUnion([Q0]), "radius" : 2 * mm, "tangentPropagation" : true, "allowEdgeOverflow" : false});
        }
        {
            var Q0;
            {var subQ0=sQuery(id+"F0.wireOp",EDGE,"E21.filletArc");var subQ1=sQuery(id+"F0.wireOp",EDGE,"E7");var subQ2=sQuery(id+"F0.wireOp",EDGE,"E6");var subQ3=sQuery(id+"F0.wireOp",EDGE,"E5");var subQ4=sQuery(id+"F0.wireOp",EDGE,"E4");var subQ5=sQuery(id+"F0.wireOp",EDGE,"E22.filletArc");var subQ6=sQuery(id+"F0.wireOp",EDGE,"E1.bottom");var subQ7=sQuery(id+"F0.wireOp",EDGE,"E1.right");var subQ8=sQuery(id+"F0.wireOp",EDGE,"E1.top");var subQ9=sQuery(id+"F0.wireOp",EDGE,"E1.left");var subQ10=sQuery(id+"F0.wireOp",EDGE,"E23.filletArc");var subQ11=sQuery(id+"F0.wireOp",EDGE,"E24.filletArc");Q0=makeQuery(id+"F2.boolean.opBoolean","SPLIT",FACE,{"disambiguationData":[TD([makeQuery(id+"F1.opExtrude","SWEPT_FACE",FACE,{"disambiguationData":[OSD([subQ6])]})])],"derivedFrom":makeQuery(id+"F1.opExtrude","CAP_FACE",FACE,{"disambiguationData":[OSD([subQ6,subQ8,subQ9,subQ7,subQ4,subQ3,subQ2,subQ1,subQ0,subQ5,subQ10,subQ11])],"isStart":true})});}
            var sketch = newSketch(context, id + "F16", { "sketchPlane" : qUnion([Q0])});
            skLineSegment(sketch, "E79.0", {"start": v(-74.25, -64.25) * mm, "end": v(-74.25, 64.25) * mm});
            skArc(sketch, "E79.1", {"start": v(-64.25, 74.25) * mm, "mid": v(-71.32, 71.32) * mm, "end": v(-74.25, 64.25) * mm});
            skLineSegment(sketch, "E79.2", {"start": v(64.25, 74.25) * mm, "end": v(-64.25, 74.25) * mm});
            skArc(sketch, "E79.3", {"start": v(74.25, 64.25) * mm, "mid": v(71.32, 71.32) * mm, "end": v(64.25, 74.25) * mm});
            skLineSegment(sketch, "E79.4", {"start": v(74.25, -64.25) * mm, "end": v(74.25, 64.25) * mm});
            skArc(sketch, "E79.5", {"start": v(64.25, -74.25) * mm, "mid": v(71.32, -71.32) * mm, "end": v(74.25, -64.25) * mm});
            skLineSegment(sketch, "E79.6", {"start": v(-64.25, -74.25) * mm, "end": v(64.25, -74.25) * mm});
            skArc(sketch, "E79.7", {"start": v(-74.25, -64.25) * mm, "mid": v(-71.32, -71.32) * mm, "end": v(-64.25, -74.25) * mm});
            skCircle(sketch, "E79.8", {"center": v(-60, -60) * mm, "radius": 4 * mm});
            skCircle(sketch, "E79.9", {"center": v(-60, 60) * mm, "radius": 4 * mm});
            skCircle(sketch, "E79.10", {"center": v(60, 60) * mm, "radius": 4 * mm});
            skCircle(sketch, "E79.11", {"center": v(60, -60) * mm, "radius": 4 * mm});
            skArc(sketch, "E79.12", {"start": v(-54.26, -47.88) * mm, "mid": v(0, -60) * mm, "end": v(54.26, -47.88) * mm});
            skArc(sketch, "E79.13", {"start": v(54.26, -47.88) * mm, "mid": v(58.44, -44.2) * mm, "end": v(60, -38.83) * mm});
            skLineSegment(sketch, "E79.14", {"start": v(60, 38.83) * mm, "end": v(60, -38.83) * mm});
            skArc(sketch, "E79.15", {"start": v(60, 38.83) * mm, "mid": v(58.44, 44.2) * mm, "end": v(54.26, 47.88) * mm});
            skArc(sketch, "E79.16", {"start": v(54.26, 47.88) * mm, "mid": v(0, 60) * mm, "end": v(-54.26, 47.88) * mm});
            skArc(sketch, "E79.17", {"start": v(-54.26, 47.88) * mm, "mid": v(-58.44, 44.2) * mm, "end": v(-60, 38.83) * mm});
            skLineSegment(sketch, "E79.18", {"start": v(-60, 38.83) * mm, "end": v(-60, -38.83) * mm});
            skArc(sketch, "E79.19", {"start": v(-60, -38.83) * mm, "mid": v(-58.44, -44.2) * mm, "end": v(-54.26, -47.88) * mm});
            skLineSegment(sketch, "E80", {"start": v(0, 74.25) * mm, "end": v(0, 104.25) * mm, "construction": true});
            skCircle(sketch, "E81", {"center": v(0, 104.25) * mm, "radius": 6 * mm});
            skArc(sketch, "E82", {"start": v(15, 104.25) * mm, "mid": v(0, 119.25) * mm, "end": v(-15, 104.25) * mm});
            skLineSegment(sketch, "E83", {"start": v(-15, 104.25) * mm, "end": v(-15, 92.25) * mm});
            skLineSegment(sketch, "E84", {"start": v(-15, 92.25) * mm, "end": v(-33, 74.25) * mm});
            skLineSegment(sketch, "E85", {"start": v(15, 104.25) * mm, "end": v(15, 92.25) * mm});
            skLineSegment(sketch, "E86", {"start": v(15, 92.25) * mm, "end": v(33, 74.25) * mm});
            skPoint(sketch, "E87", {"position": v(-74.25, 0) * mm});
            skPoint(sketch, "E88", {"position": v(74.25, 0) * mm});
            skLineSegment(sketch, "E89", {"start": v(-74.25, 0) * mm, "end": v(74.25, 0) * mm, "construction": true});
            skLineSegment(sketch, "E90.MirrorCS", {"start": v(-15, -92.25) * mm, "end": v(-33, -74.25) * mm});
            skLineSegment(sketch, "E91.MirrorCS", {"start": v(-15, -104.25) * mm, "end": v(-15, -92.25) * mm});
            skArc(sketch, "E92.MirrorCS", {"start": v(15, -104.25) * mm, "mid": v(0, -119.25) * mm, "end": v(-15, -104.25) * mm});
            skCircle(sketch, "E93.MirrorC", {"center": v(0, -104.25) * mm, "radius": 6 * mm});
            skLineSegment(sketch, "E94.MirrorCS", {"start": v(0, -74.25) * mm, "end": v(0, -104.25) * mm, "construction": true});
            skLineSegment(sketch, "E95.MirrorCS", {"start": v(15, -92.25) * mm, "end": v(33, -74.25) * mm});
            skLineSegment(sketch, "E96.MirrorCS", {"start": v(15, -104.25) * mm, "end": v(15, -92.25) * mm});
            skSolve(sketch);
        }
        {
            var Q0;
            Q0 = qSketchRegion(id + "F16", true);
            var Q1;
            Q1=makeQuery(id+"F2.opExtrude","CAP_FACE",FACE,{"disambiguationData":[OSD([sQuery(id+"F0.wireOp",EDGE,"E12"),sQuery(id+"F0.wireOp",EDGE,"E13"),sQuery(id+"F0.wireOp",EDGE,"E14"),sQuery(id+"F0.wireOp",EDGE,"E15"),sQuery(id+"F0.wireOp",EDGE,"E17.filletArc"),sQuery(id+"F0.wireOp",EDGE,"E18.filletArc"),sQuery(id+"F0.wireOp",EDGE,"E19.filletArc"),sQuery(id+"F0.wireOp",EDGE,"E20.filletArc"),sQuery(id+"F0.wireOp",EDGE,"E25.0"),sQuery(id+"F0.wireOp",EDGE,"E25.1"),sQuery(id+"F0.wireOp",EDGE,"E25.2"),sQuery(id+"F0.wireOp",EDGE,"E25.3"),sQuery(id+"F0.wireOp",EDGE,"E25.4"),sQuery(id+"F0.wireOp",EDGE,"E25.5"),sQuery(id+"F0.wireOp",EDGE,"E25.6"),sQuery(id+"F0.wireOp",EDGE,"E25.7")])],"isStart":false});
            extrude(context, id + "F17", {"entities" : qUnion([Q0]), "endBound" : BoundingType.UP_TO_SURFACE, "endBoundEntityFace" : qUnion([Q1]), "depth" : 25 * mm});
        }
    });
